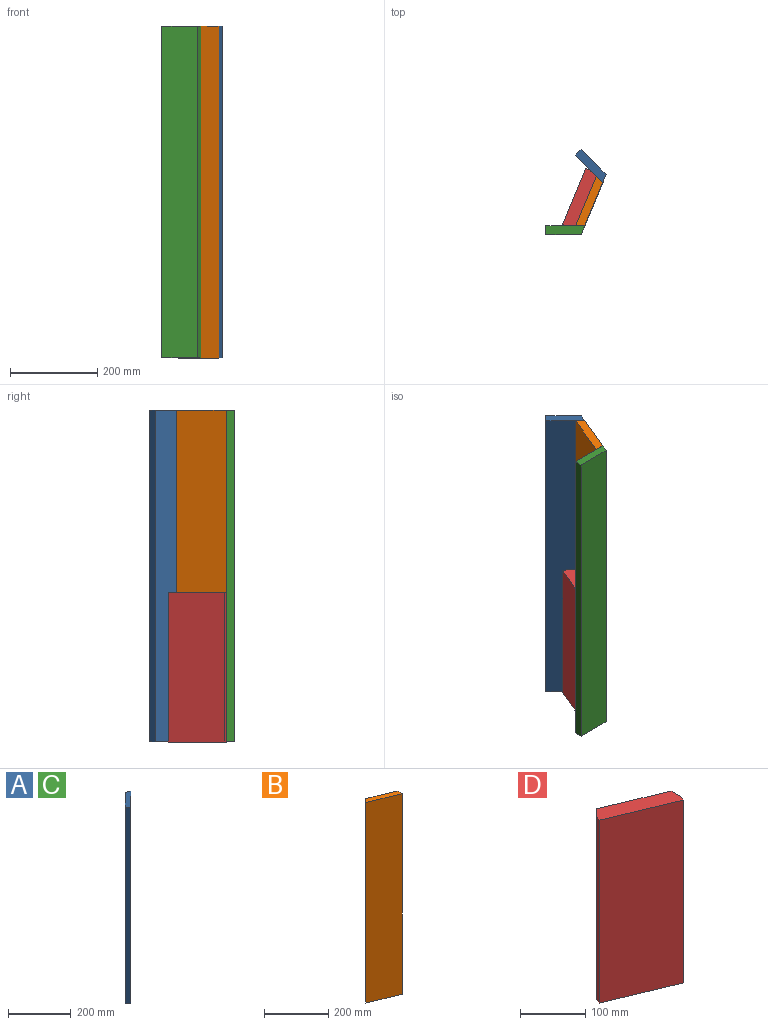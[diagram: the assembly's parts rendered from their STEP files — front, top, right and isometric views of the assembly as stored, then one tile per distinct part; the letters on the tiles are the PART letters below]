
ASSEMBLY  parts=4 mates=3
PART A: 6 faces, bbox 76.3x70.8x762 mm
  f0: plane 762x62.86mm, normal (0.71,-0.71,0), area 67741.8mm2, adj f1,f3,f4,f5
  f1: plane 762x19.05mm, normal (0.38,0.92,0), area 15712.1mm2, adj f0,f2,f4,f5
  f2: plane 762x57.28mm, normal (-0.71,0.71,0), area 61729mm2, adj f1,f3,f4,f5
  f3: plane 762x13.47mm, normal (-0.71,-0.71,0), area 14516.1mm2, adj f0,f2,f4,f5
  f4: plane 76.33x70.75mm, normal (0,0,1), area 1618.4mm2, adj f0,f1,f2,f3
  f5: plane 76.33x70.75mm, normal (0,0,-1), area 1618.4mm2, adj f0,f1,f2,f3
PART B: 6 faces, bbox 114.3x61.9x762 mm
  f0: plane 762x14.58mm, normal (-0.71,0.71,0), area 15712.1mm2, adj f1,f3,f4,f5
  f1: plane 762x114.3mm, normal (-0.38,-0.92,0), area 94272.7mm2, adj f0,f2,f4,f5
  f2: plane 762x20.62mm, normal (1,0,0), area 15712.1mm2, adj f1,f3,f4,f5
  f3: plane 762x99.72mm, normal (0.38,0.92,0), area 82247.1mm2, adj f0,f2,f4,f5
  f4: plane 114.3x61.93mm, normal (0,0,1), area 2206.5mm2, adj f0,f1,f2,f3
  f5: plane 114.3x61.93mm, normal (0,0,-1), area 2206.5mm2, adj f0,f1,f2,f3
PART C: same geometry as A
PART D: 8 faces, bbox 132.9x77.5x342.9 mm
  f0: plane 342.9x20.88mm, normal (1,0,0), area 7160.5mm2, adj f1,f5,f6,f7
  f1: plane 342.9x114.3mm, normal (0.38,0.92,0), area 42422.7mm2, adj f0,f2,f6,f7
  f2: plane 342.9x14.77mm, normal (-0.71,0.71,0), area 7160.5mm2, adj f1,f3,f6,f7
  f3: plane 342.9x9.31mm, normal (-0.92,0.38,0), area 3455.1mm2, adj f2,f4,f6,f7
  f4: plane 342.9x129.07mm, normal (-0.38,-0.92,0), area 47903.1mm2, adj f3,f5,f6,f7
  f5: plane 342.9x9.31mm, normal (0.92,-0.38,0), area 3455.1mm2, adj f0,f4,f6,f7
  f6: plane 132.92x77.54mm, normal (0,0,-1), area 3948.6mm2, adj f0,f1,f2,f3,f4,f5
  f7: plane 132.92x77.54mm, normal (0,0,1), area 3948.6mm2, adj f0,f1,f2,f3,f4,f5
PLACE A rot(axis=(0,0,-1),90deg) t=(-1242.16,1317.95,0)mm
PLACE B rot(axis=(0,0,-1),90deg) t=(-1242.16,1317.95,0)mm
PLACE C rot(axis=(0.92,0.38,0),180deg) t=(-1810.27,-53.59,762)mm
PLACE D rot(axis=(0,0,-1),90deg) t=(-1162.86,1224.88,342.9)mm
MATE fastened A.f0 <-> B.f0  axis (-0.71,-0.71,0) through (29.65,46.13,762)mm
MATE fastened D.f1 <-> B.f1  axis (0.92,-0.38,0) through (-8.6,3.56,0)mm
MATE fastened B.f2 <-> C.f0  axis (0,-1,0) through (-11.65,-53.59,762)mm
